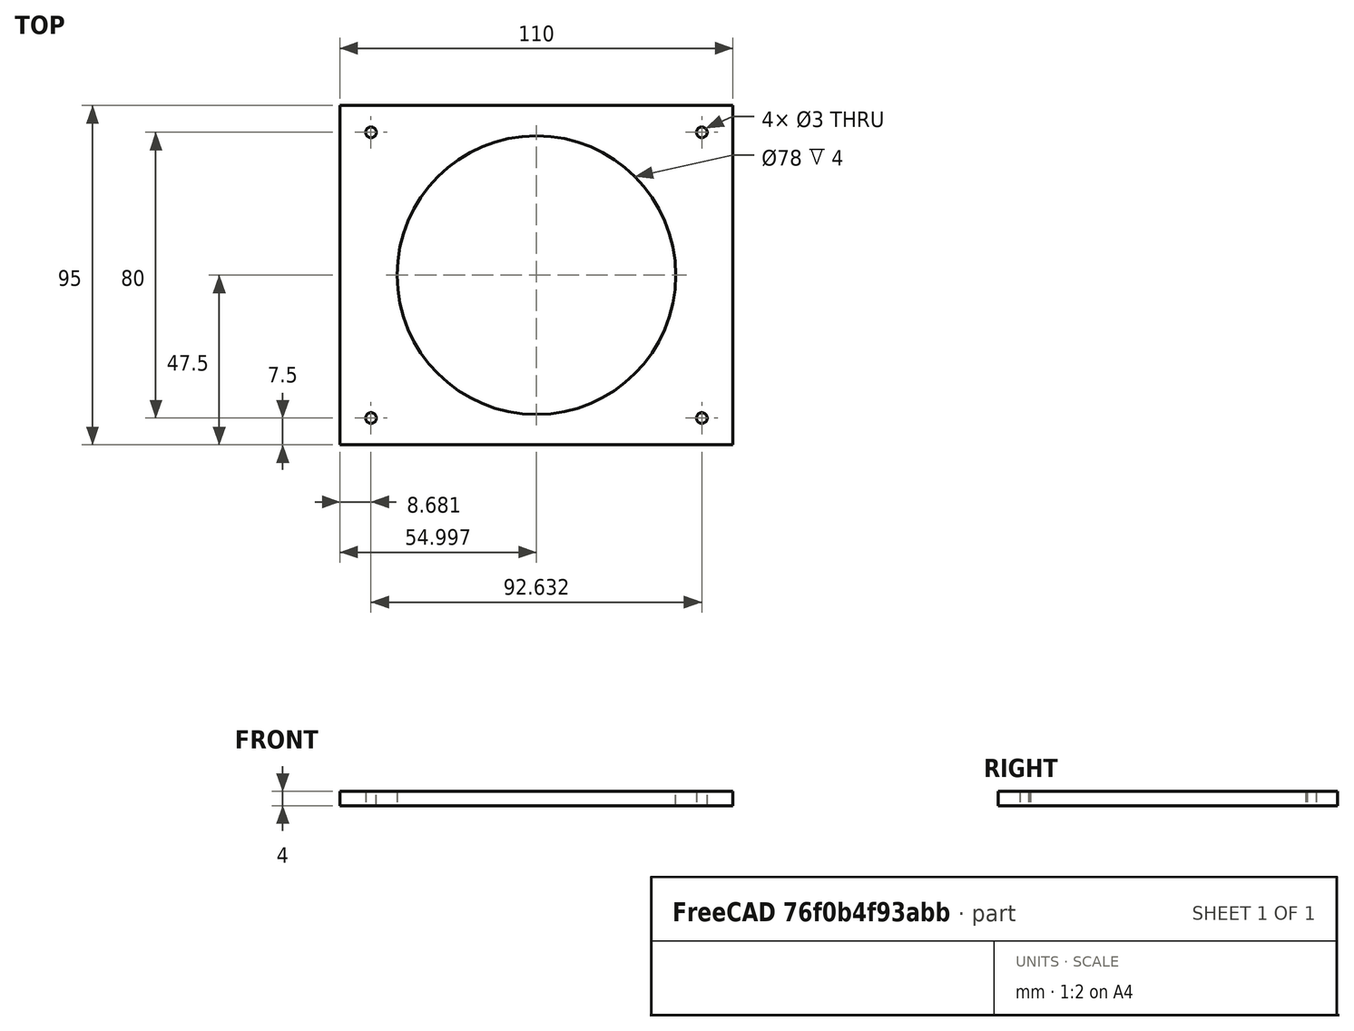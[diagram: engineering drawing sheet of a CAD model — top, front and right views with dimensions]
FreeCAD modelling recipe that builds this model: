
FCSTD DOCUMENT  (FreeCAD 1.0R39319 (Git))
Label: stearing_Flange
License: All rights reserved
LicenseURL: https://en.wikipedia.org/wiki/All_rights_reserved
objects: Sketcher::SketchObject×3, PartDesign::Pad×1, PartDesign::Body×1
note: 10 computed .brp shape members not serialized (recipe doc carries the construction recipe); baked Part::Feature solids carry a one-line shape summary decoded from their .brp

FEATURE [Sketcher::SketchObject] Sketch001
  ArcFitTolerance = 1e-06
  AttachmentSupport = -> [XY_Plane]
  FullyConstrained = false
  MakeInternals = false
  MapMode = 5
  sketch-geometry (8):
    g0: LineSegment StartX=0 StartY=4.263e-13 StartZ=0 EndX=186.825 EndY=4.263e-13 EndZ=0
    g1: LineSegment StartX=250 StartY=63.1748 StartZ=0 EndX=250 EndY=83.3235 EndZ=0
    g2: LineSegment StartX=183.324 StartY=150 StartZ=0 EndX=0 EndY=150 EndZ=0
    g3: LineSegment StartX=0 StartY=150 StartZ=0 EndX=0 EndY=4.263e-13 EndZ=0
    g4: ArcOfCircle CenterX=183.324 CenterY=83.3235 CenterZ=0 NormalX=0 NormalY=0 NormalZ=1 AngleXU=0 Radius=66.6765 StartAngle=0 EndAngle=1.5708
    g5: GeomPoint [constr] X=250 Y=150 Z=0
    g6: ArcOfCircle CenterX=186.825 CenterY=63.1748 CenterZ=0 NormalX=0 NormalY=0 NormalZ=1 AngleXU=0 Radius=63.1748 StartAngle=4.71239 EndAngle=6.28319
    g7: GeomPoint [constr] X=250 Y=0 Z=0
  constraints (17):
    c: Coincident(g2,g3)
    c: Coincident(g3,g0)
    c: Horizontal(g0)
    c: Horizontal(g2)
    c: Vertical(g1)
    c: Vertical(g3)
    c: Coincident(g0,g-1)
    c: DistanceX(g2,g5) = 250
    c: DistanceY(g3,g3) = 150
    c: PointOnObject(g5,g2)
    c: PointOnObject(g5,g1)
    c: Tangent(g2,g4) = -1.5708
    c: Tangent(g1,g4) = -1.5708
    c: PointOnObject(g7,g0)
    c: PointOnObject(g7,g1)
    c: Tangent(g0,g6) = -1.5708
    c: Tangent(g1,g6) = -1.5708
FEATURE [Sketcher::SketchObject] Sketch
  ArcFitTolerance = 1e-06
  FullyConstrained = false
  MakeInternals = false
  MapMode = 5
  Placement = pos=(0,0,4) rot=(0,0,1;0rad)
  sketch-geometry (18):
    g0: Circle [constr] CenterX=172.107 CenterY=75 CenterZ=0 NormalX=0 NormalY=0 NormalZ=1 AngleXU=0 Radius=42.5
    g1: LineSegment [constr] StartX=172.107 StartY=75 StartZ=0 EndX=172.107 EndY=150 EndZ=0
    g2: LineSegment [constr] StartX=172.107 StartY=75 StartZ=0 EndX=172.107 EndY=0 EndZ=0
    g3: LineSegment [constr] StartX=172.107 StartY=75 StartZ=0 EndX=172.107 EndY=85 EndZ=0
    g4: LineSegment [constr] StartX=172.107 StartY=75 StartZ=0 EndX=172.107 EndY=65 EndZ=0
    g5: LineSegment StartX=172.107 StartY=65 StartZ=0 EndX=203.107 EndY=65 EndZ=0
    g6: LineSegment StartX=207.107 StartY=69 StartZ=0 EndX=207.107 EndY=81 EndZ=0
    g7: LineSegment StartX=203.107 StartY=85 StartZ=0 EndX=172.107 EndY=85 EndZ=0
    g8: LineSegment StartX=172.107 StartY=85 StartZ=0 EndX=141.107 EndY=85 EndZ=0
    g9: LineSegment StartX=137.107 StartY=81 StartZ=0 EndX=137.107 EndY=69 EndZ=0
    g10: LineSegment StartX=141.107 StartY=65 StartZ=0 EndX=172.107 EndY=65 EndZ=0
    g11: Circle CenterX=172.107 CenterY=75 CenterZ=0 NormalX=0 NormalY=0 NormalZ=1 AngleXU=0 Radius=41
    g12: ArcOfCircle CenterX=141.107 CenterY=81 CenterZ=0 NormalX=0 NormalY=0 NormalZ=1 AngleXU=0 Radius=4 StartAngle=1.5708 EndAngle=3.14159
    g13: ArcOfCircle CenterX=141.107 CenterY=69 CenterZ=0 NormalX=0 NormalY=0 NormalZ=1 AngleXU=0 Radius=4 StartAngle=3.14159 EndAngle=4.71239
    g14: ArcOfCircle CenterX=203.107 CenterY=69 CenterZ=0 NormalX=0 NormalY=0 NormalZ=1 AngleXU=0 Radius=4 StartAngle=4.71239 EndAngle=6.28319
    g15: ArcOfCircle CenterX=203.107 CenterY=81 CenterZ=0 NormalX=0 NormalY=0 NormalZ=1 AngleXU=0 Radius=4 StartAngle=-9e-16 EndAngle=1.5708
    g16: LineSegment [constr] StartX=141.107 StartY=85 StartZ=0 EndX=172.107 EndY=112.5 EndZ=0
    g17: LineSegment [constr] StartX=172.107 StartY=112.5 StartZ=0 EndX=203.107 EndY=85 EndZ=0
  constraints (44):
    c: Diameter(g0) = 85
    c: Coincident(g1,g0)
    c: PointOnObject(g1,g-3)
    c: Vertical(g1)
    c: Coincident(g2,g0)
    c: PointOnObject(g2,g-4)
    c: Vertical(g2)
    c: Equal(g2,g1)
    c: Coincident(g3,g0)
    c: PointOnObject(g3,g1)
    c: Coincident(g4,g0)
    c: PointOnObject(g4,g2)
    c: Coincident(g5,g4)
    c: Horizontal(g5)
    c: Vertical(g6)
    c: Coincident(g7,g3)
    c: Horizontal(g7)
    c: Coincident(g8,g3)
    c: Horizontal(g8)
    c: Vertical(g9)
    c: Coincident(g10,g4)
    c: Horizontal(g10)
    c: Equal(g4,g3)
    c: Coincident(g11,g0)
    c: Diameter(g11) = 82
    c: Tangent(g9,g12) = -1.5708
    c: Tangent(g8,g12) = -1.5708
    c: Tangent(g9,g13) = -1.5708
    c: Tangent(g10,g13) = -1.5708
    c: Tangent(g5,g14) = -1.5708
    c: Tangent(g6,g14) = -1.5708
    c: Tangent(g6,g15) = -1.5708
    c: Tangent(g7,g15) = -1.5708
    c: Equal(g12,g13)
    c: Equal(g13,g14)
    c: Equal(g14,g15)
    c: Radius(g12) = 4
    c: DistanceY(g4,g3) = 20
    c: DistanceX(g9,g6) = 70
    c: Coincident(g16,g8)
    c: Symmetric(g1,g1,g16)
    c: Coincident(g17,g16)
    c: Coincident(g17,g7)
    c: Equal(g17,g16)
FEATURE [Sketcher::SketchObject] Sketch002
  ArcFitTolerance = 1e-06
  AttachmentSupport = -> [XY_Plane]
  ExternalGeometry = -> [Sketch]
  FullyConstrained = true
  MakeInternals = false
  MapMode = 5
  sketch-geometry (18):
    g0: Circle CenterX=172.107 CenterY=75 CenterZ=0 NormalX=0 NormalY=0 NormalZ=1 AngleXU=0 Radius=39
    g1: LineSegment StartX=117.107 StartY=122.5 StartZ=0 EndX=117.107 EndY=27.5 EndZ=0
    g2: LineSegment StartX=117.107 StartY=27.5 StartZ=0 EndX=227.107 EndY=27.5 EndZ=0
    g3: LineSegment StartX=227.107 StartY=27.5 StartZ=0 EndX=227.107 EndY=122.5 EndZ=0
    g4: LineSegment StartX=227.107 StartY=122.5 StartZ=0 EndX=117.107 EndY=122.5 EndZ=0
    g5: LineSegment [constr] StartX=172.107 StartY=75 StartZ=0 EndX=227.107 EndY=122.5 EndZ=0
    g6: LineSegment [constr] StartX=172.107 StartY=75 StartZ=0 EndX=117.107 EndY=122.5 EndZ=0
    g7: LineSegment [constr] StartX=117.107 StartY=27.5 StartZ=0 EndX=172.107 EndY=75 EndZ=0
    g8: LineSegment [constr] StartX=172.107 StartY=75 StartZ=0 EndX=227.107 EndY=27.5 EndZ=0
    g9: LineSegment [constr] StartX=172.107 StartY=75 StartZ=0 EndX=172.107 EndY=116 EndZ=0
    g10: Circle CenterX=218.423 CenterY=115 CenterZ=0 NormalX=0 NormalY=0 NormalZ=1 AngleXU=0 Radius=1.5
    g11: Circle CenterX=218.423 CenterY=35 CenterZ=0 NormalX=0 NormalY=0 NormalZ=1 AngleXU=0 Radius=1.5
    g12: Circle CenterX=125.791 CenterY=35 CenterZ=0 NormalX=0 NormalY=0 NormalZ=1 AngleXU=0 Radius=1.5
    g13: Circle CenterX=125.791 CenterY=115 CenterZ=0 NormalX=0 NormalY=0 NormalZ=1 AngleXU=0 Radius=1.5
    g14: LineSegment [constr] StartX=125.791 StartY=115 StartZ=0 EndX=125.791 EndY=35 EndZ=0
    g15: LineSegment [constr] StartX=125.791 StartY=35 StartZ=0 EndX=218.423 EndY=35 EndZ=0
    g16: LineSegment [constr] StartX=218.423 StartY=35 StartZ=0 EndX=218.423 EndY=115 EndZ=0
    g17: LineSegment [constr] StartX=218.423 StartY=115 StartZ=0 EndX=125.791 EndY=115 EndZ=0
  constraints (48):
    c: Coincident(g0,g-3)
    c: Coincident(g1,g2)
    c: Coincident(g2,g3)
    c: Coincident(g3,g4)
    c: Coincident(g4,g1)
    c: Vertical(g1)
    c: Vertical(g3)
    c: Horizontal(g2)
    c: Horizontal(g4)
    c: Coincident(g5,g0)
    c: Coincident(g5,g3)
    c: Coincident(g6,g0)
    c: Coincident(g6,g1)
    c: Coincident(g7,g1)
    c: Coincident(g7,g0)
    c: Coincident(g8,g0)
    c: Coincident(g8,g2)
    c: Equal(g5,g8)
    c: PointOnObject(g9,g7)
    c: PointOnObject(g9,g-3)
    c: Vertical(g9)
    c: DistanceY(g9,g1) = 6.5
    c: Diameter(g0) = 78
    c: DistanceY(g3,g3) = 95
    c: DistanceX(g4,g4) = 110
    c: PointOnObject(g10,g5)
    c: PointOnObject(g11,g8)
    c: PointOnObject(g12,g7)
    c: PointOnObject(g13,g6)
    c: Equal(g13,g10)
    c: Equal(g10,g11)
    c: Diameter(g10) = 3
    c: Equal(g12,g11)
    c: Coincident(g14,g15)
    c: Coincident(g15,g16)
    c: Coincident(g16,g17)
    c: Coincident(g17,g14)
    c: Vertical(g14)
    c: Vertical(g16)
    c: Horizontal(g15)
    c: Horizontal(g17)
    c: Coincident(g14,g13)
    c: Coincident(g15,g11)
    c: Coincident(g16,g10)
    c: PointOnObject(g12,g15)
    c: Parallel(g7,g5)
    c: PointOnObject(g9,g8)
    c: DistanceY(g16,g16) = 80
FEATURE [PartDesign::Pad] Pad
  Direction = (0,0,1)
  Length = 4
  Length2 = 10
  Profile = -> Sketch002
  ReferenceAxis = -> Sketch002 [N_Axis]
  Refine = true
  Suppressed = false
  Type = 0
FEATURE [PartDesign::Body] Body
  AllowCompound = false
  Group = -> [Sketch001,Sketch,Sketch002,Pad]
  Origin = -> Origin
  Tip = -> Pad
